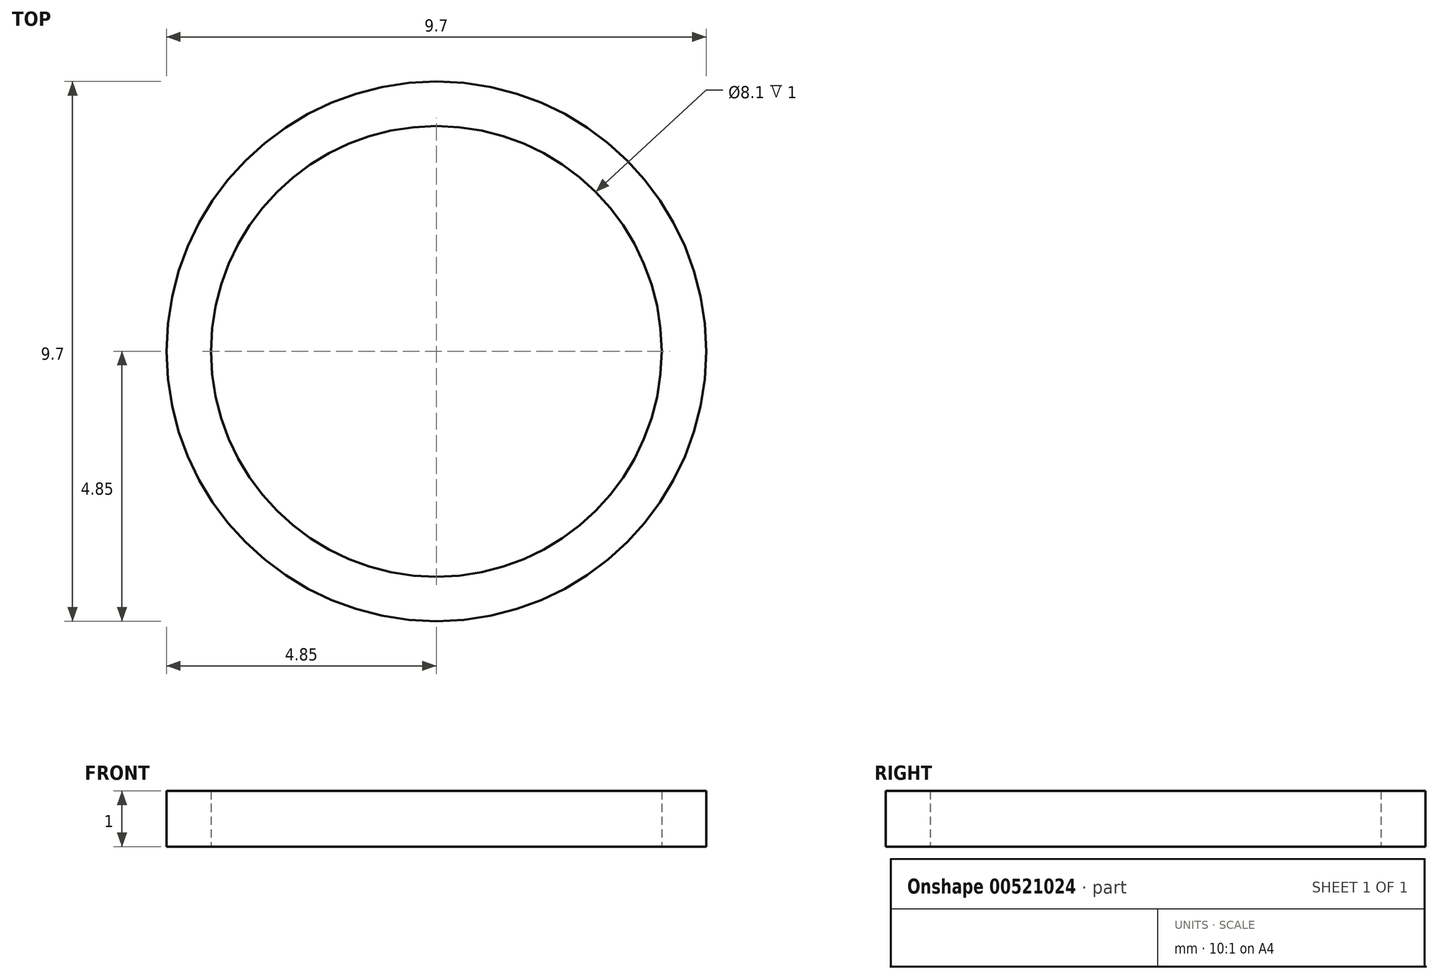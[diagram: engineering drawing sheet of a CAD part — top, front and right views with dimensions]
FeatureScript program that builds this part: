
annotation { "Feature Type Name" : "Feature", "Feature Type Description" : "" }
export const myFeature = defineFeature(function(context is Context, id is Id, definition is map)
    precondition{}
    {
        {
            var Q0;
            Q0=qCreatedBy(makeId("Top.planeOp"),FACE);
            var sketch = newSketch(context, id + "F0", { "sketchPlane" : qUnion([Q0])});
            skCircle(sketch, "E0", {"center": v(0, 0) * mm, "radius": 4.05 * mm});
            skCircle(sketch, "E1", {"center": v(0, 0) * mm, "radius": 4.85 * mm});
            skSolve(sketch);
        }
        {
            var Q0;
            Q0=makeQuery(id+"F0.imprint","IMPRINT",FACE,{"disambiguationData":[TD([[makeQuery(id+"F0.imprint","IMPRINT",EDGE,{"derivedFrom":sQuery(id+"F0.wireOp",EDGE,"E0")}),-1.0]])]});
            extrude(context, id + "F1", {"entities" : qUnion([Q0]), "depth" : 1 * mm, "offsetDistance" : 25 * mm});
        }
    });
